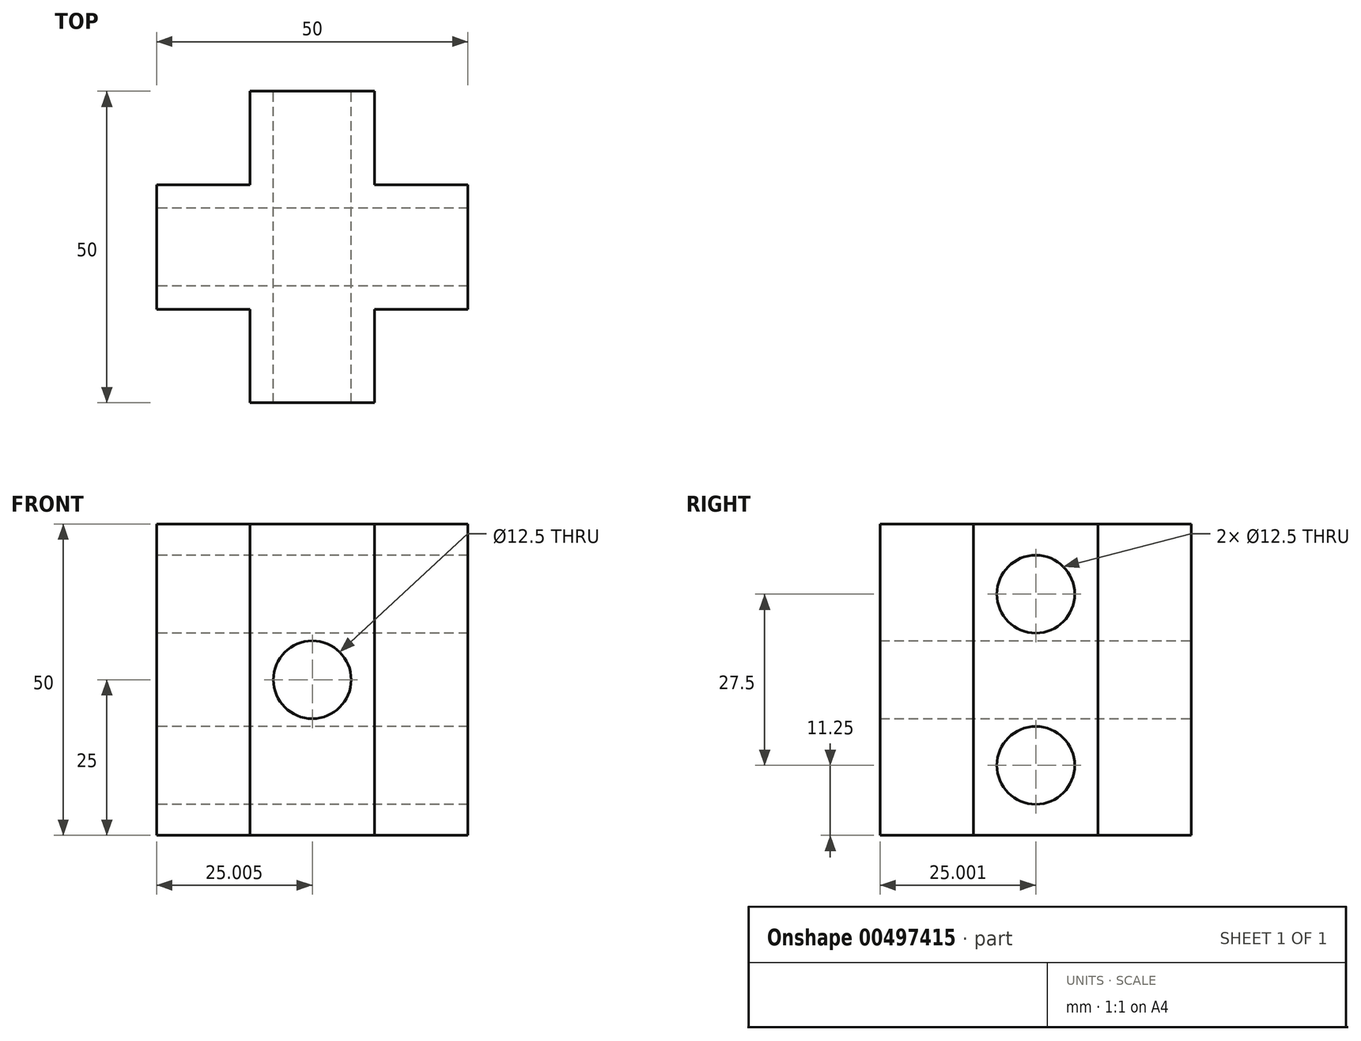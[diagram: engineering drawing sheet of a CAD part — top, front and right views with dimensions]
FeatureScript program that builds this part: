
annotation { "Feature Type Name" : "Feature", "Feature Type Description" : "" }
export const myFeature = defineFeature(function(context is Context, id is Id, definition is map)
    precondition{}
    {
        {
            var Q0;
            Q0=qCreatedBy(makeId("Top.planeOp"),FACE);
            var sketch = newSketch(context, id + "F0", { "sketchPlane" : qUnion([Q0])});
            skLineSegment(sketch, "E0.bottom", {"start": v(-66.76, 2.96) * mm, "end": v(-16.76, 2.96) * mm});
            skLineSegment(sketch, "E0.top", {"start": v(-66.76, -47.04) * mm, "end": v(-16.76, -47.04) * mm});
            skLineSegment(sketch, "E0.left", {"start": v(-66.76, 2.96) * mm, "end": v(-66.76, -47.04) * mm});
            skLineSegment(sketch, "E0.right", {"start": v(-16.76, 2.96) * mm, "end": v(-16.76, -47.04) * mm});
            skSolve(sketch);
        }
        {
            var Q0;
            Q0=makeQuery(id+"F0.imprint","IMPRINT",FACE,{"disambiguationData":[TD([[makeQuery(id+"F0.imprint","IMPRINT",EDGE,{"derivedFrom":sQuery(id+"F0.wireOp",EDGE,"E0.bottom")}),-1.0]])]});
            extrude(context, id + "F1", {"entities" : qUnion([Q0]), "depth" : 50 * mm});
        }
        {
            var Q0;
            Q0=makeQuery(id+"F1.opExtrude","SWEPT_FACE",FACE,{"disambiguationData":[OSD([sQuery(id+"F0.wireOp",EDGE,"E0.left")])]});
            var sketch = newSketch(context, id + "F2", { "sketchPlane" : qUnion([Q0])});
            skCircle(sketch, "E1", {"center": v(22.04, 38.75) * mm, "radius": 6.25 * mm});
            skPoint(sketch, "E1.centerSnap0", {"position": v(22.04, 50) * mm});
            skCircle(sketch, "E2", {"center": v(22.04, 11.25) * mm, "radius": 6.25 * mm});
            skPoint(sketch, "E2.centerSnap0", {"position": v(22.04, 0) * mm});
            skSolve(sketch);
        }
        {
            var Q0;
            Q0=makeQuery(id+"F2.imprint","IMPRINT",FACE,{"disambiguationData":[TD([[makeQuery(id+"F2.imprint","IMPRINT",EDGE,{"derivedFrom":sQuery(id+"F2.wireOp",EDGE,"E1")}),1.0]])]});
            extrude(context, id + "F3", {"entities" : qUnion([Q0]), "operationType" : NewBodyOperationType.REMOVE, "endBound" : BoundingType.THROUGH_ALL, "oppositeDirection" : true, "depth" : 25 * mm});
        }
        {
            var Q0;
            Q0=makeQuery(id+"F1.opExtrude","SWEPT_FACE",FACE,{"disambiguationData":[OSD([sQuery(id+"F0.wireOp",EDGE,"E0.left")])]});
            var sketch = newSketch(context, id + "F4", { "sketchPlane" : qUnion([Q0])});
            skCircle(sketch, "E3", {"center": v(22.04, 11.25) * mm, "radius": 6.25 * mm});
            skPoint(sketch, "E3.centerSnap0", {"position": v(22.04, 0) * mm});
            skSolve(sketch);
        }
        {
            var Q0;
            Q0=makeQuery(id+"F4.imprint","IMPRINT",FACE,{"disambiguationData":[TD([[makeQuery(id+"F4.imprint","IMPRINT",EDGE,{"derivedFrom":sQuery(id+"F4.wireOp",EDGE,"E3")}),1.0]])]});
            extrude(context, id + "F5", {"entities" : qUnion([Q0]), "operationType" : NewBodyOperationType.REMOVE, "endBound" : BoundingType.THROUGH_ALL, "oppositeDirection" : true, "depth" : 25 * mm});
        }
        {
            var Q0;
            Q0=makeQuery(id+"F1.opExtrude","SWEPT_FACE",FACE,{"disambiguationData":[OSD([sQuery(id+"F0.wireOp",EDGE,"E0.bottom")])]});
            var sketch = newSketch(context, id + "F6", { "sketchPlane" : qUnion([Q0])});
            skCircle(sketch, "E4", {"center": v(41.76, 25) * mm, "radius": 6.25 * mm});
            skPoint(sketch, "E4.centerSnap0", {"position": v(16.76, 25) * mm});
            skPoint(sketch, "E4.centerSnap1", {"position": v(41.76, 0) * mm});
            skSolve(sketch);
        }
        {
            var Q0;
            Q0=makeQuery(id+"F6.imprint","IMPRINT",FACE,{"disambiguationData":[TD([[makeQuery(id+"F6.imprint","IMPRINT",EDGE,{"derivedFrom":sQuery(id+"F6.wireOp",EDGE,"E4")}),1.0]])]});
            extrude(context, id + "F7", {"entities" : qUnion([Q0]), "operationType" : NewBodyOperationType.REMOVE, "endBound" : BoundingType.THROUGH_ALL, "oppositeDirection" : true, "depth" : 25 * mm});
        }
        {
            var Q0;
            Q0=makeQuery(id+"F1.opExtrude","CAP_FACE",FACE,{"disambiguationData":[OSD([sQuery(id+"F0.wireOp",EDGE,"E0.bottom"),sQuery(id+"F0.wireOp",EDGE,"E0.top"),sQuery(id+"F0.wireOp",EDGE,"E0.left"),sQuery(id+"F0.wireOp",EDGE,"E0.right")])],"isStart":false});
            var sketch = newSketch(context, id + "F8", { "sketchPlane" : qUnion([Q0])});
            skLineSegment(sketch, "E5.bottom", {"start": v(-66.76, -47.04) * mm, "end": v(-51.76, -47.04) * mm});
            skLineSegment(sketch, "E5.top", {"start": v(-66.76, -32.04) * mm, "end": v(-51.76, -32.04) * mm});
            skLineSegment(sketch, "E5.left", {"start": v(-66.76, -47.04) * mm, "end": v(-66.76, -32.04) * mm});
            skLineSegment(sketch, "E5.right", {"start": v(-51.76, -47.04) * mm, "end": v(-51.76, -32.04) * mm});
            skSolve(sketch);
        }
        {
            var Q0;
            Q0=makeQuery(id+"F8.imprint","IMPRINT",FACE,{"disambiguationData":[TD([[makeQuery(id+"F8.imprint","IMPRINT",EDGE,{"derivedFrom":sQuery(id+"F8.wireOp",EDGE,"E5.bottom")}),1.0]])]});
            extrude(context, id + "F9", {"entities" : qUnion([Q0]), "operationType" : NewBodyOperationType.REMOVE, "endBound" : BoundingType.THROUGH_ALL, "oppositeDirection" : true, "depth" : 25 * mm});
        }
        {
            var Q0;
            Q0=makeQuery(id+"F1.opExtrude","CAP_FACE",FACE,{"disambiguationData":[OSD([sQuery(id+"F0.wireOp",EDGE,"E0.bottom"),sQuery(id+"F0.wireOp",EDGE,"E0.top"),sQuery(id+"F0.wireOp",EDGE,"E0.left"),sQuery(id+"F0.wireOp",EDGE,"E0.right")])],"isStart":false});
            var sketch = newSketch(context, id + "F10", { "sketchPlane" : qUnion([Q0])});
            skLineSegment(sketch, "E6.bottom", {"start": v(-66.76, 2.96) * mm, "end": v(-51.76, 2.96) * mm});
            skLineSegment(sketch, "E6.top", {"start": v(-66.76, -12.04) * mm, "end": v(-51.76, -12.04) * mm});
            skLineSegment(sketch, "E6.left", {"start": v(-66.76, 2.96) * mm, "end": v(-66.76, -12.04) * mm});
            skLineSegment(sketch, "E6.right", {"start": v(-51.76, 2.96) * mm, "end": v(-51.76, -12.04) * mm});
            skSolve(sketch);
        }
        {
            var Q0;
            Q0=makeQuery(id+"F10.imprint","IMPRINT",FACE,{"disambiguationData":[TD([[makeQuery(id+"F10.imprint","IMPRINT",EDGE,{"derivedFrom":sQuery(id+"F10.wireOp",EDGE,"E6.bottom")}),-1.0]])]});
            extrude(context, id + "F11", {"entities" : qUnion([Q0]), "operationType" : NewBodyOperationType.REMOVE, "endBound" : BoundingType.THROUGH_ALL, "oppositeDirection" : true, "depth" : 25 * mm});
        }
        {
            var Q0;
            Q0=makeQuery(id+"F1.opExtrude","CAP_FACE",FACE,{"disambiguationData":[OSD([sQuery(id+"F0.wireOp",EDGE,"E0.bottom"),sQuery(id+"F0.wireOp",EDGE,"E0.top"),sQuery(id+"F0.wireOp",EDGE,"E0.left"),sQuery(id+"F0.wireOp",EDGE,"E0.right")])],"isStart":false});
            var sketch = newSketch(context, id + "F12", { "sketchPlane" : qUnion([Q0])});
            skLineSegment(sketch, "E7.bottom", {"start": v(-16.76, 2.96) * mm, "end": v(-31.76, 2.96) * mm});
            skLineSegment(sketch, "E7.top", {"start": v(-16.76, -12.04) * mm, "end": v(-31.76, -12.04) * mm});
            skLineSegment(sketch, "E7.left", {"start": v(-16.76, 2.96) * mm, "end": v(-16.76, -12.04) * mm});
            skLineSegment(sketch, "E7.right", {"start": v(-31.76, 2.96) * mm, "end": v(-31.76, -12.04) * mm});
            skSolve(sketch);
        }
        {
            var Q0;
            Q0=makeQuery(id+"F12.imprint","IMPRINT",FACE,{"disambiguationData":[TD([[makeQuery(id+"F12.imprint","IMPRINT",EDGE,{"derivedFrom":sQuery(id+"F12.wireOp",EDGE,"E7.bottom")}),-1.0]])]});
            extrude(context, id + "F13", {"entities" : qUnion([Q0]), "operationType" : NewBodyOperationType.REMOVE, "endBound" : BoundingType.THROUGH_ALL, "oppositeDirection" : true, "depth" : 25 * mm});
        }
        {
            var Q0;
            Q0=makeQuery(id+"F1.opExtrude","CAP_FACE",FACE,{"disambiguationData":[OSD([sQuery(id+"F0.wireOp",EDGE,"E0.bottom"),sQuery(id+"F0.wireOp",EDGE,"E0.top"),sQuery(id+"F0.wireOp",EDGE,"E0.left"),sQuery(id+"F0.wireOp",EDGE,"E0.right")])],"isStart":false});
            var sketch = newSketch(context, id + "F14", { "sketchPlane" : qUnion([Q0])});
            skLineSegment(sketch, "E8.bottom", {"start": v(-16.76, -47.04) * mm, "end": v(-31.76, -47.04) * mm});
            skLineSegment(sketch, "E8.top", {"start": v(-16.76, -32.04) * mm, "end": v(-31.76, -32.04) * mm});
            skLineSegment(sketch, "E8.left", {"start": v(-16.76, -47.04) * mm, "end": v(-16.76, -32.04) * mm});
            skLineSegment(sketch, "E8.right", {"start": v(-31.76, -47.04) * mm, "end": v(-31.76, -32.04) * mm});
            skSolve(sketch);
        }
        {
            var Q0;
            Q0=makeQuery(id+"F14.imprint","IMPRINT",FACE,{"disambiguationData":[TD([[makeQuery(id+"F14.imprint","IMPRINT",EDGE,{"derivedFrom":sQuery(id+"F14.wireOp",EDGE,"E8.bottom")}),1.0]])]});
            extrude(context, id + "F15", {"entities" : qUnion([Q0]), "operationType" : NewBodyOperationType.REMOVE, "endBound" : BoundingType.THROUGH_ALL, "oppositeDirection" : true, "depth" : 25 * mm});
        }
    });
